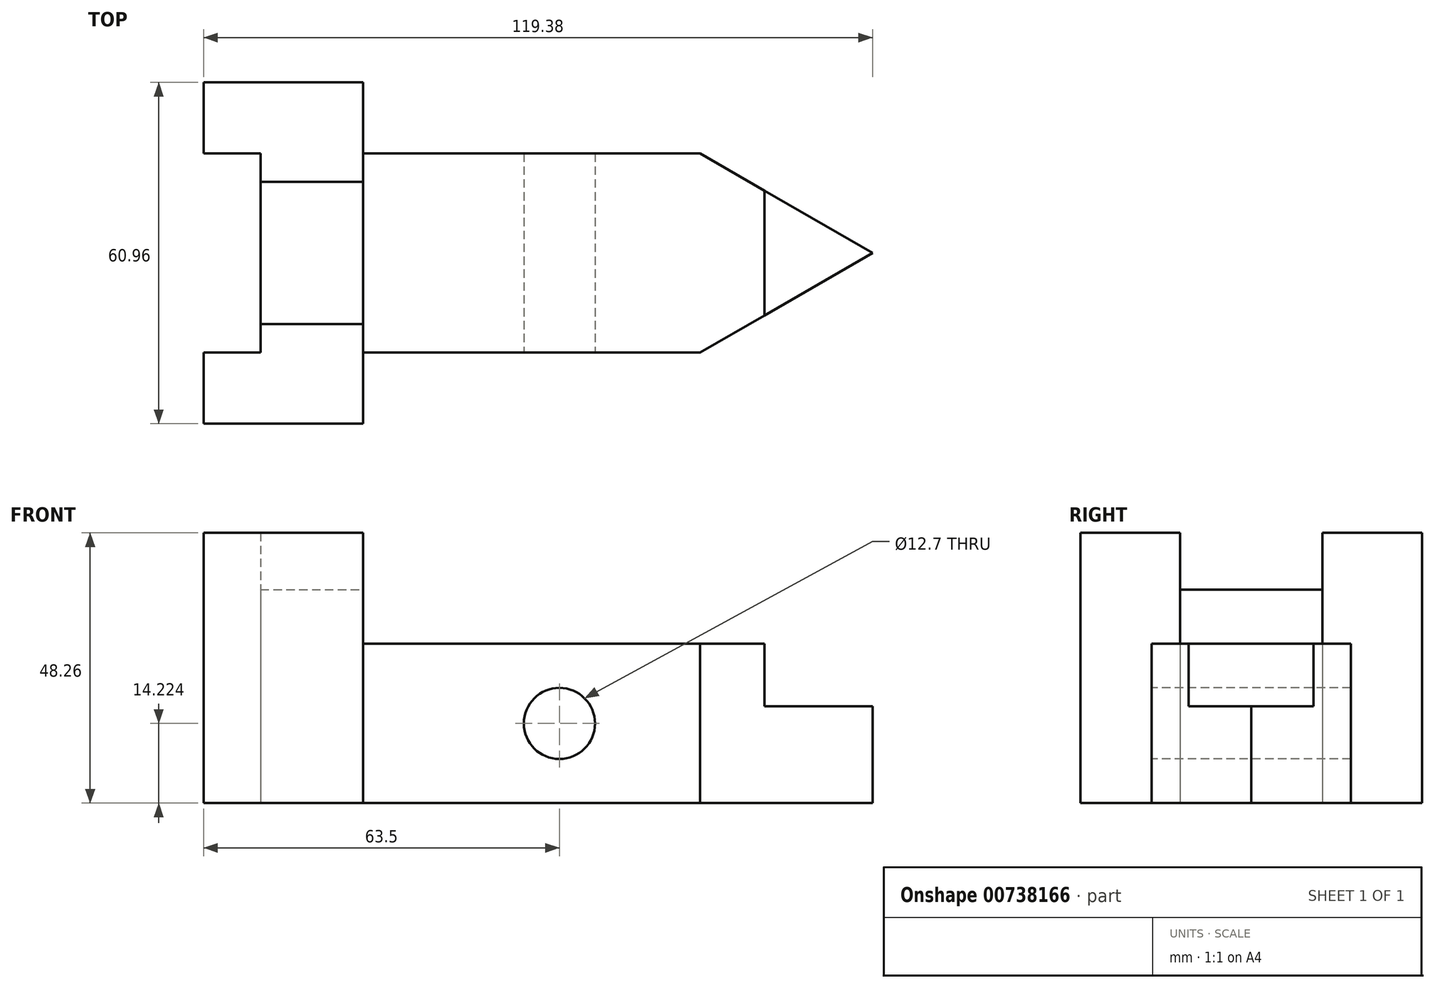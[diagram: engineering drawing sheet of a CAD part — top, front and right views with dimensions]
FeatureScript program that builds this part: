
annotation { "Feature Type Name" : "Feature", "Feature Type Description" : "" }
export const myFeature = defineFeature(function(context is Context, id is Id, definition is map)
    precondition{}
    {
        {
            var Q0;
            Q0=qCreatedBy(makeId("Top.planeOp"),FACE);
            var sketch = newSketch(context, id + "F0", { "sketchPlane" : qUnion([Q0])});
            skLineSegment(sketch, "E0", {"start": v(-65.62, 17.78) * mm, "end": v(-55.46, 17.78) * mm});
            skLineSegment(sketch, "E1", {"start": v(-55.46, 17.78) * mm, "end": v(-37.17, 17.78) * mm});
            skLineSegment(sketch, "E2", {"start": v(-37.17, 17.78) * mm, "end": v(-37.17, -43.18) * mm});
            skLineSegment(sketch, "E3", {"start": v(-37.17, -43.18) * mm, "end": v(-55.46, -43.18) * mm});
            skLineSegment(sketch, "E4", {"start": v(-55.46, -43.18) * mm, "end": v(-65.62, -43.18) * mm});
            skLineSegment(sketch, "E5", {"start": v(-65.62, -43.18) * mm, "end": v(-65.62, -30.48) * mm});
            skLineSegment(sketch, "E6", {"start": v(-65.62, -30.48) * mm, "end": v(-55.46, -30.48) * mm});
            skLineSegment(sketch, "E7", {"start": v(-55.46, -30.48) * mm, "end": v(-55.46, -25.4) * mm});
            skLineSegment(sketch, "E8", {"start": v(-65.62, 17.78) * mm, "end": v(-65.62, 5.08) * mm});
            skLineSegment(sketch, "E9", {"start": v(-65.62, 5.08) * mm, "end": v(-55.46, 5.08) * mm});
            skLineSegment(sketch, "E10", {"start": v(-55.46, 5.08) * mm, "end": v(-55.46, 0) * mm});
            skLineSegment(sketch, "E11", {"start": v(-55.46, 0) * mm, "end": v(-55.46, -25.4) * mm});
            skLineSegment(sketch, "E12", {"start": v(-55.46, -25.4) * mm, "end": v(-37.17, -25.4) * mm});
            skLineSegment(sketch, "E13", {"start": v(-55.46, 0) * mm, "end": v(-37.17, 0) * mm});
            skLineSegment(sketch, "E14", {"start": v(-37.17, -12.7) * mm, "end": v(-37.17, -30.48) * mm});
            skLineSegment(sketch, "E15", {"start": v(-37.17, -30.48) * mm, "end": v(-37.17, -12.7) * mm});
            skLineSegment(sketch, "E16", {"start": v(-37.17, -12.7) * mm, "end": v(-37.17, 5.08) * mm});
            skLineSegment(sketch, "E17", {"start": v(-37.17, 5.08) * mm, "end": v(-37.17, -12.7) * mm});
            skLineSegment(sketch, "E18", {"start": v(53.76, -12.7) * mm, "end": v(22.96, 5.08) * mm});
            skLineSegment(sketch, "E19", {"start": v(53.76, -12.7) * mm, "end": v(22.96, -30.48) * mm});
            skLineSegment(sketch, "E20", {"start": v(-37.17, 5.08) * mm, "end": v(22.96, 5.08) * mm});
            skLineSegment(sketch, "E21", {"start": v(-37.17, -30.48) * mm, "end": v(22.96, -30.48) * mm});
            skLineSegment(sketch, "E22", {"start": v(34.46, -12.7) * mm, "end": v(34.46, -1.55) * mm});
            skLineSegment(sketch, "E23", {"start": v(34.46, -1.55) * mm, "end": v(34.46, -23.85) * mm});
            skSolve(sketch);
        }
        {
            var Q0;
            {var subQ0=sQuery(id+"F0.wireOp",EDGE,"E3");Q0=makeQuery(id+"F0.imprint","IMPRINT",FACE,{"disambiguationData":[TD([[makeQuery(id+"F0.imprint","IMPRINT",EDGE,{"derivedFrom":subQ0}),-1.0]])]});}
            var Q1;
            Q1=makeQuery(id+"F0.imprint","IMPRINT",FACE,{"disambiguationData":[TD([[makeQuery(id+"F0.imprint","IMPRINT",EDGE,{"derivedFrom":sQuery(id+"F0.wireOp",EDGE,"E0")}),-1.0]])]});
            extrude(context, id + "F1", {"entities" : qUnion([Q0, Q1]), "depth" : 48.26 * mm, "offsetDistance" : 25.4 * mm});
        }
        {
            var Q0;
            Q0=makeQuery(id+"F0.imprint","IMPRINT",FACE,{"disambiguationData":[TD([[makeQuery(id+"F0.imprint","IMPRINT",EDGE,{"derivedFrom":sQuery(id+"F0.wireOp",EDGE,"E11")}),1.0]])]});
            extrude(context, id + "F2", {"entities" : qUnion([Q0]), "depth" : 38.1 * mm, "offsetDistance" : 25.4 * mm});
        }
        {
            var Q0;
            {var subQ4=sQuery(id+"F0.wireOp",EDGE,"E20");Q0=makeQuery(id+"F0.imprint","IMPRINT",FACE,{"disambiguationData":[TD([[makeQuery(id+"F0.imprint","IMPRINT",EDGE,{"derivedFrom":subQ4}),-1.0]])]});}
            extrude(context, id + "F3", {"entities" : qUnion([Q0]), "depth" : 28.45 * mm, "offsetDistance" : 25.4 * mm});
        }
        {
            var Q0;
            {var subQ3=sQuery(id+"F0.wireOp",EDGE,"E23");var subQ6=makeQuery(id+"F0.imprint","IMPRINT",VERTEX,{"derivedFrom":subQ3});Q0=makeQuery(id+"F0.imprint","IMPRINT",FACE,{"disambiguationData":[TD([[makeQuery(id+"F0.imprint","IMPRINT",EDGE,{"disambiguationData":[TD([[subQ6,1.0]])],"derivedFrom":subQ3}),1.0]])]});}
            extrude(context, id + "F4", {"entities" : qUnion([Q0]), "operationType" : NewBodyOperationType.ADD, "depth" : 17.27 * mm, "offsetDistance" : 25.4 * mm});
        }
        {
            var Q0;
            Q0=makeQuery(id+"F3.opExtrude","SWEPT_FACE",FACE,{"disambiguationData":[OSD([sQuery(id+"F0.wireOp",EDGE,"E21")])]});
            var sketch = newSketch(context, id + "F5", { "sketchPlane" : qUnion([Q0])});
            skCircle(sketch, "E24", {"center": v(-2.12, 14.22) * mm, "radius": 6.35 * mm});
            skSolve(sketch);
        }
        {
            var Q0;
            Q0=makeQuery(id+"F5.imprint","IMPRINT",FACE,{"disambiguationData":[TD([[makeQuery(id+"F5.imprint","IMPRINT",EDGE,{"derivedFrom":sQuery(id+"F5.wireOp",EDGE,"E24")}),1.0]])]});
            extrude(context, id + "F6", {"entities" : qUnion([Q0]), "operationType" : NewBodyOperationType.REMOVE, "oppositeDirection" : true, "depth" : 71.12 * mm, "offsetDistance" : 25.4 * mm});
        }
    });
